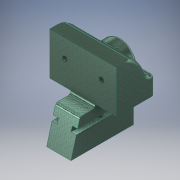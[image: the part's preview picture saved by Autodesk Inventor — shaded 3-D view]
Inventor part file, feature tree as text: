
AUTODESK INVENTOR PART (.ipt)
format: ipt  version: 2017 (Build 210142000, 142)  size: 352,256 bytes
history: native  units: in
note: dims shown in document units (in); Inventor stores cm internally (conversion verified against a paired STEP export)
features: hole x7, extrude x4, sketch x4, fillet x2
ambient origin geometry x8: Origin, YZ Plane, XZ Plane, XY Plane, X Axis, Y Axis, Z Axis, Center Point
bodies: Solid1 (feature_tree)
feature tree (17):
  extrude  "Extrusion1"  Depth=0.75in
  extrude  "Extrusion2"  Depth=1.1875in
  extrude  "Extrusion3"  Depth=0.125in
  extrude  "Extrusion4"  Depth=0.125in TaperAngle=0.0deg
  hole  "Hole1"  [1 undecoded]
  hole  "Hole2"  [1 undecoded]
  hole  "Hole3"  [1 undecoded]
  hole  "Hole4"  [1 undecoded]
  hole  "Hole5"  [1 undecoded]
  hole  "Hole6"  [1 undecoded]
  hole  "Hole7"  [1 undecoded]
  fillet  "Fillet1"  Radius=0.5055in
  fillet  "Fillet2"  Radius=2.5625in
  sketch  "Sketch1"  dims[d0=1.75in d1=0.75in]
  sketch  "Sketch2"  dims[d2=1.5625in d3=1.1875in]
  sketch  "Sketch3"  dims[d5=0.125in d6=1.375in]
  sketch  "Sketch5"  dims[d7=0.25in d8=2.75in d9=0.0in d10=1.375in d11=0.875in d13=2.1875in d16=0.875in d17=1.5in d18=0.2175in d19=0.1875in d20=0.5055in d21=2.5625in d22=0.0in d23=1.75in d24=1.0in d25=2.75in d26=0.0in d27=1.375in d28=0.375in d29=0.125in d30=0.125in d31=2.75in d32=0.0in d33=1.188in d34=0.1875in d35=0.1495in d36=0.432in d37=0.142in d38=0.141in d39=90.0deg d40=1.0625in d41=0.0in d42=1.1875in d43=0.1875in d44=0.1495in d45=0.432in d46=0.142in d47=0.141in d48=90.0deg d49=1.0625in d50=0.0in d51=1.0in d52=1.0in d53=0.171in d54=0.432in d55=0.2188in d56=0.375in d57=90.0deg d58=0.75in d59=0.0in d60=1.0in d61=1.0in d62=0.171in d63=0.432in d64=0.2188in d65=0.375in d66=90.0deg d67=0.75in d68=0.0in d78=1.0in d79=1.0in d71=0.758in d72=1.625in d73=0.142in d74=1.1875in d75=90.0deg d76=0.4375in d77=0.0in d80=1.0in d81=0.625in d82=0.196in d83=0.625in d84=0.375in d85=0.25in d86=0.5635in d87=0.625in d88=0.8108in d89=1.0in d90=0.625in d91=0.196in d92=0.625in d93=0.375in d94=0.25in d95=0.5635in d96=0.625in d97=0.8108in d98=0.25in d99=0.125in d100=0.125in]
note: 7 required parameter values undecoded (feature->parameter linkage not recoverable at this tier; creation-order binding heuristic only, values carry confidence <= 0.55)
